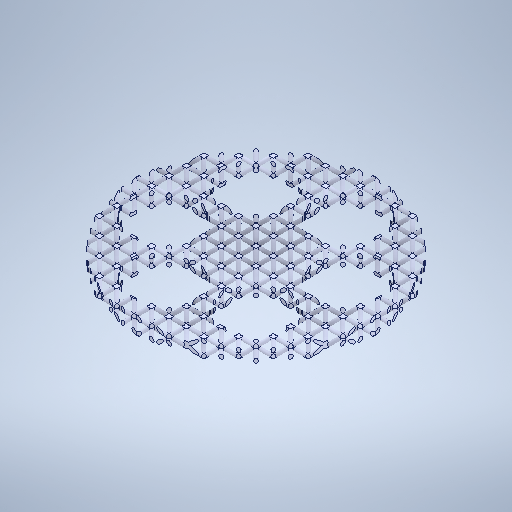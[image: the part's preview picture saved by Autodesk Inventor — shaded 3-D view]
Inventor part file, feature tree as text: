
AUTODESK INVENTOR PART (.ipt)
format: ipt  version: 2025.3 (Build 293356000, 356)  size: 4,044,288 bytes
history: native  units: in
note: dims shown in document units (in); Inventor stores cm internally (conversion verified against a paired STEP export)
features: extrude x2, sketch x2, projected_geometry x2, pattern_linear x1, plane x1, other x1
ambient origin geometry x8: Origin, YZ Plane, XZ Plane, XY Plane, X Axis, Y Axis, Z Axis, Center Point
bodies: Solid1 (feature_tree)
feature tree (9):
  pattern_linear  "Rectangular Pattern1"  Count1=14 Spacing1=0.315in
  plane  "Work Plane1"
  extrude  "Extrusion1"  Depth=2.3622in
  extrude  "Extrusion3"  Depth=1.1811in
  sketch  "Sketch1"  dims[d6=4.3307in d7=2.3622in]
  sketch  "Sketch2"  dims[d8=1.1811in d9=1.1811in d10=1.1811in d11=1.1811in d12=1.1811in d13=1.1811in d14=4.3307in d15=0.0in d16=4.3307in d19=4.3307in d20=0.0in d17=0.0197in d18=1.9685in]
  other  "Cut-Extrude14"
  projected_geometry  "Project Cut Edges1"
  projected_geometry  "Project Cut Edges2"
